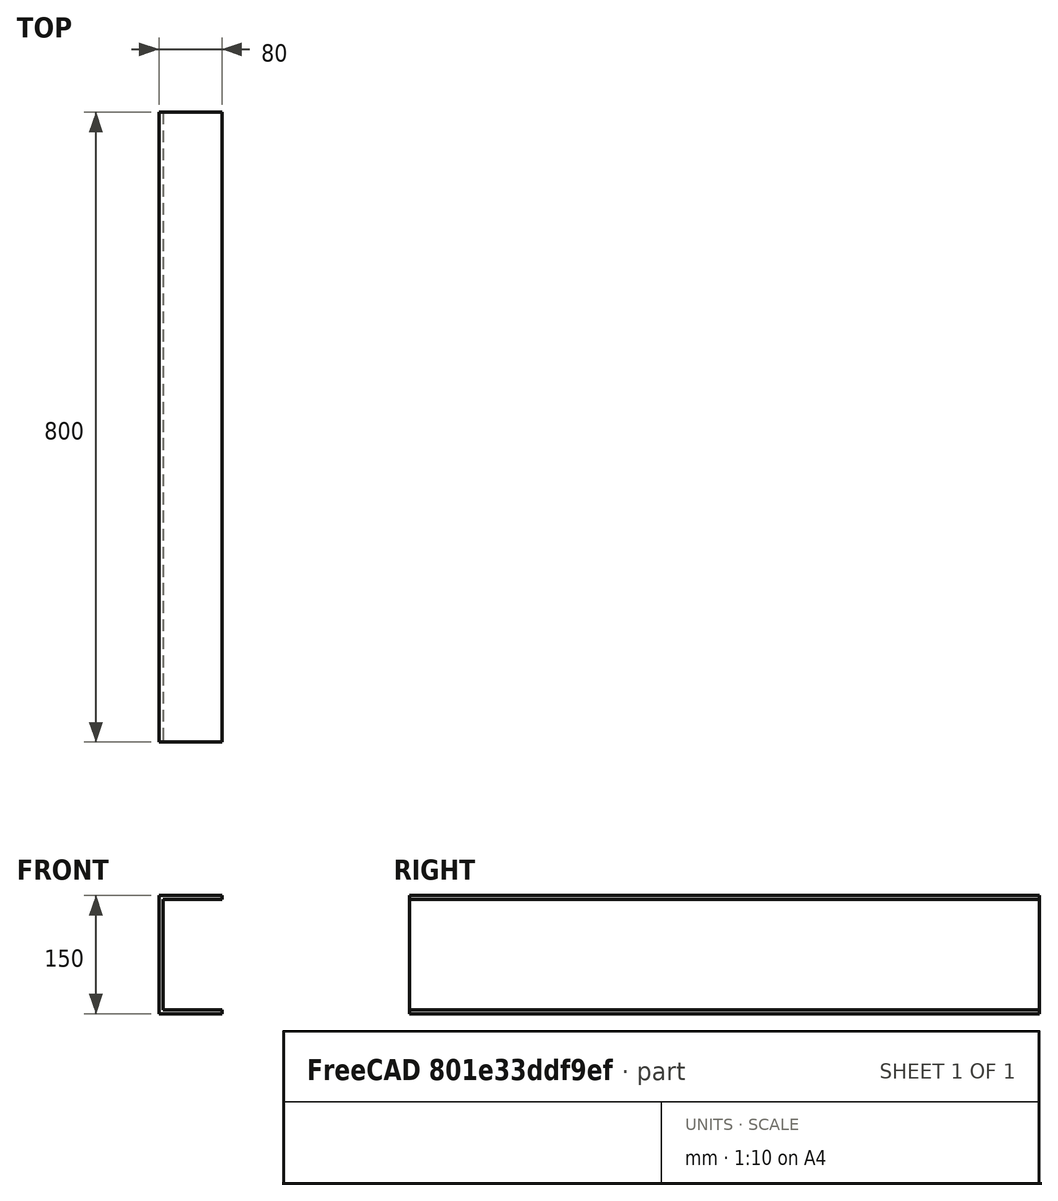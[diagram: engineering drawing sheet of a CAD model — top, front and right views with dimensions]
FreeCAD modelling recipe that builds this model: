
FCSTD DOCUMENT  (FreeCAD 0.19R24366 (Git))
Label: C_Section_800
License: All rights reserved
LicenseURL: http://en.wikipedia.org/wiki/All_rights_reserved
objects: Sketcher::SketchObject×2, PartDesign::Pad×1, PartDesign::Body×1
note: 5 computed .brp shape members not serialized (recipe doc carries the construction recipe); baked Part::Feature solids carry a one-line shape summary decoded from their .brp

FEATURE [Sketcher::SketchObject] Sketch
  FullyConstrained = true
  MapMode = 5
  Support = -> [XY_Plane]
FEATURE [Sketcher::SketchObject] Sketch001
  FullyConstrained = false
  MapMode = 5
  Placement = pos=(0,0,0) rot=(1,0,0;1.5708rad)
  Support = -> [XZ_Plane]
  sketch-geometry (8):
    g0: LineSegment StartX=34.9026 StartY=82.6599 StartZ=0 EndX=-45.0974 EndY=82.6599 EndZ=0
    g1: LineSegment StartX=-45.0974 StartY=82.6599 StartZ=0 EndX=-45.0974 EndY=-67.3401 EndZ=0
    g2: LineSegment StartX=-45.0974 StartY=-67.3401 StartZ=0 EndX=34.9026 EndY=-67.3401 EndZ=0
    g3: LineSegment StartX=34.9026 StartY=-67.3401 StartZ=0 EndX=34.9026 EndY=-62.3401 EndZ=0
    g4: LineSegment StartX=34.9026 StartY=-62.3401 StartZ=0 EndX=-40.0974 EndY=-62.3401 EndZ=0
    g5: LineSegment StartX=-40.0974 StartY=-62.3401 StartZ=0 EndX=-40.0974 EndY=77.6599 EndZ=0
    g6: LineSegment StartX=-40.0974 StartY=77.6599 StartZ=0 EndX=34.9026 EndY=77.6599 EndZ=0
    g7: LineSegment StartX=34.9026 StartY=77.6599 StartZ=0 EndX=34.9026 EndY=82.6599 EndZ=0
  constraints (22):
    c: Horizontal(g0)
    c: Coincident(g0,g1)
    c: Vertical(g1)
    c: Coincident(g1,g2)
    c: Horizontal(g2)
    c: Coincident(g2,g3)
    c: Vertical(g3)
    c: Coincident(g3,g4)
    c: Horizontal(g4)
    c: Coincident(g4,g5)
    c: Vertical(g5)
    c: Coincident(g5,g6)
    c: Horizontal(g6)
    c: Coincident(g6,g7)
    c: Coincident(g7,g0)
    c: DistanceY(g1,g0) = 150
    c: DistanceY(g5,g5) = 140
    c: DistanceX(g4,g3) = 75
    c: DistanceX(g0,g0) = 80
    c: DistanceX(g2,g2) = 80
    c: DistanceX(g6,g6) = 75
    c: DistanceY(g3,g3) = 5
FEATURE [PartDesign::Pad] Pad
  Direction = (1,1,1)
  Length = 800
  Length2 = 100
  Placement = pos=(0,0,0) rot=(1,0,0;1.5708rad)
  Profile = -> Sketch001
  Type = 0
FEATURE [PartDesign::Body] Body
  Group = -> [Sketch,Sketch001,Pad]
  Origin = -> Origin
  Tip = -> Pad
